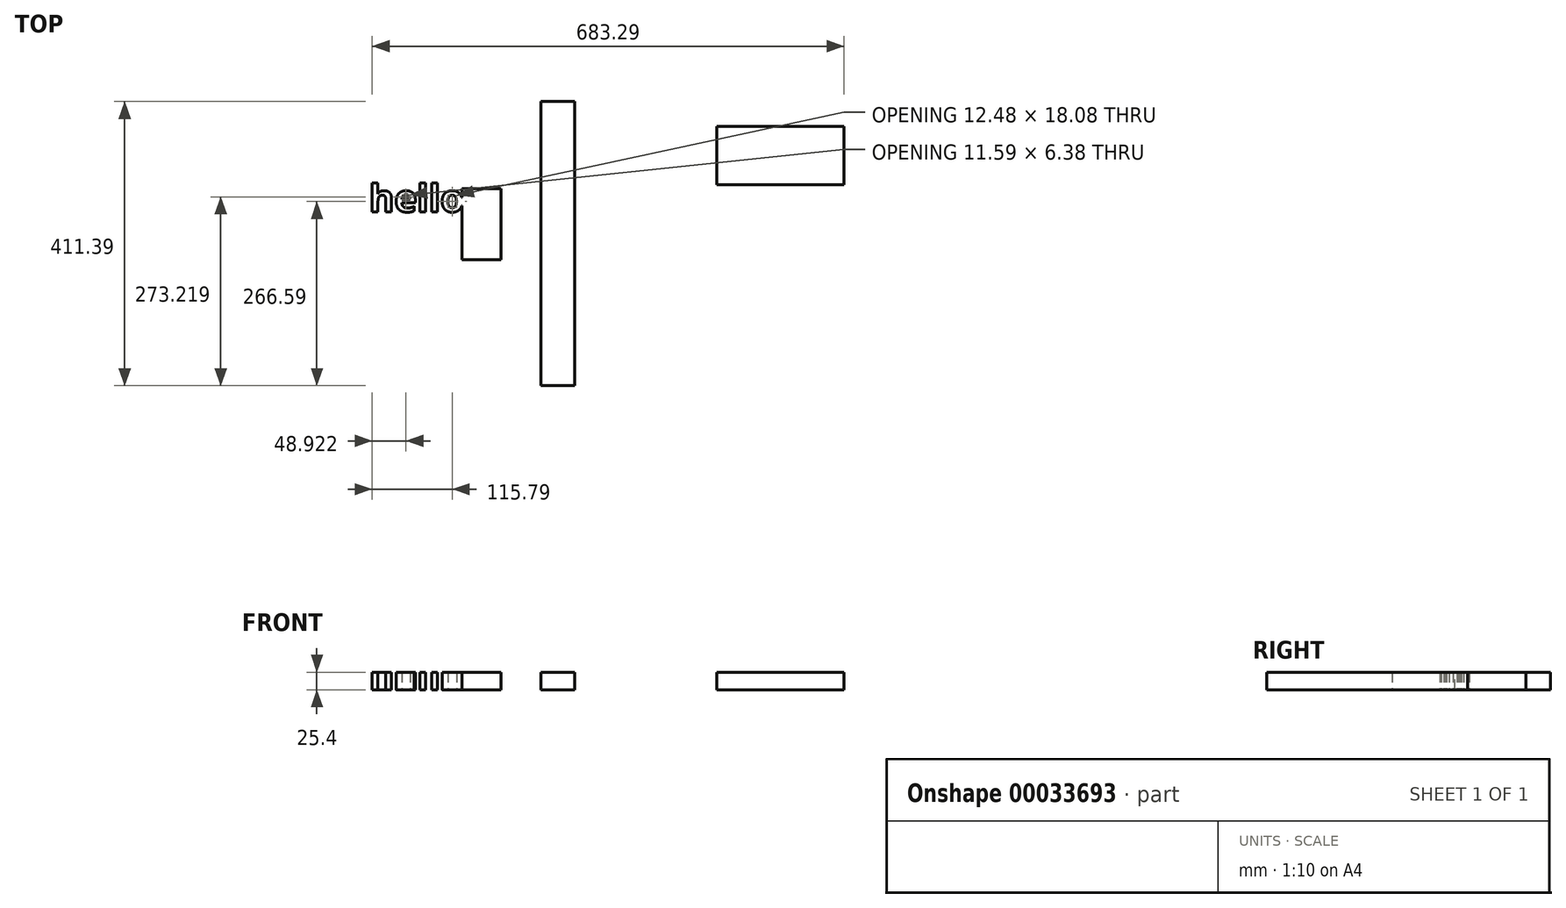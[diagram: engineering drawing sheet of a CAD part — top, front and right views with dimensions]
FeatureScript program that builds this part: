
annotation { "Feature Type Name" : "Feature", "Feature Type Description" : "" }
export const myFeature = defineFeature(function(context is Context, id is Id, definition is map)
    precondition{}
    {
        {
            var Q0;
            Q0=qCreatedBy(makeId("Top.planeOp"),FACE);
            var sketch = newSketch(context, id + "F0", { "sketchPlane" : qUnion([Q0])});
            skLineSegment(sketch, "E0.bottom", {"start": v(-276.57, -28.11) * mm, "end": v(-219.75, -28.11) * mm});
            skLineSegment(sketch, "E0.top", {"start": v(-276.57, 74.9) * mm, "end": v(-219.75, 74.9) * mm});
            skLineSegment(sketch, "E0.left", {"start": v(-276.57, -28.11) * mm, "end": v(-276.57, 74.9) * mm});
            skLineSegment(sketch, "E0.right", {"start": v(-219.75, -28.11) * mm, "end": v(-219.75, 74.9) * mm});
            skLineSegment(sketch, "E1", {"start": v(-341.55, -122.68) * mm, "end": v(-195.38, -122.68) * mm});
            skLineSegment(sketch, "E2", {"start": v(-336.67, 51.28) * mm, "end": v(-341.55, -122.68) * mm});
            skLineSegment(sketch, "E3.bottom", {"start": v(92.37, 165.15) * mm, "end": v(277.06, 165.15) * mm});
            skLineSegment(sketch, "E3.top", {"start": v(92.37, 80.88) * mm, "end": v(277.06, 80.88) * mm});
            skLineSegment(sketch, "E3.left", {"start": v(92.37, 165.15) * mm, "end": v(92.37, 80.88) * mm});
            skLineSegment(sketch, "E3.right", {"start": v(277.06, 165.15) * mm, "end": v(277.06, 80.88) * mm});
            skLineSegment(sketch, "E4", {"start": v(-171.67, 200.64) * mm, "end": v(-171.67, -206) * mm});
            skLineSegment(sketch, "E5.bottom", {"start": v(-162.07, 201.12) * mm, "end": v(-113.25, 201.12) * mm});
            skLineSegment(sketch, "E5.top", {"start": v(-162.07, -210.27) * mm, "end": v(-113.25, -210.27) * mm});
            skLineSegment(sketch, "E5.left", {"start": v(-162.07, 201.12) * mm, "end": v(-162.07, -210.27) * mm});
            skLineSegment(sketch, "E5.right", {"start": v(-113.25, 201.12) * mm, "end": v(-113.25, -210.27) * mm});
            skText(sketch, "E6", { "text": "\nhello\n", "fontName": "OpenSans-Bold.ttf"});
            const initialGuessF0  = {"E6": [-0.41056, 0.11656, 1, 0, 0.0399]};
            skSetInitialGuess(sketch, initialGuessF0);
            skSolve(sketch);
        }
        {
            var Q0;
            Q0=makeQuery(id+"F0.imprint","IMPRINT",FACE,{"disambiguationData":[TD([[makeQuery(id+"F0.imprint","IMPRINT",EDGE,{"derivedFrom":sQuery(id+"F0.wireOp",EDGE,"E3.bottom")}),-1.0]])]});
            var Q1;
            Q1=makeQuery(id+"F0.imprint","IMPRINT",FACE,{"disambiguationData":[TD([[makeQuery(id+"F0.imprint","IMPRINT",EDGE,{"derivedFrom":sQuery(id+"F0.wireOp",EDGE,"E5.bottom")}),-1.0]])]});
            var Q2;
            Q2=makeQuery(id+"F0.imprint","IMPRINT",FACE,{"disambiguationData":[TD([[makeQuery(id+"F0.imprint","IMPRINT",EDGE,{"derivedFrom":sQuery(id+"F0.wireOp",EDGE,"E6.sketch_text.stroke-0")}),-1.0]])]});
            var Q3;
            {var subQ0=sQuery(id+"F0.wireOp",EDGE,"E6.sketch_text.stroke-38");Q3=makeQuery(id+"F0.imprint","IMPRINT",FACE,{"disambiguationData":[TD([[makeQuery(id+"F0.imprint","IMPRINT",EDGE,{"derivedFrom":subQ0}),-1.0]])]});}
            var Q4;
            Q4=makeQuery(id+"F0.imprint","IMPRINT",FACE,{"disambiguationData":[TD([[makeQuery(id+"F0.imprint","IMPRINT",EDGE,{"derivedFrom":sQuery(id+"F0.wireOp",EDGE,"E6.sketch_text.stroke-41")}),-1.0]])]});
            var Q5;
            {var subQ1=sQuery(id+"F0.wireOp",EDGE,"E0.bottom");Q5=makeQuery(id+"F0.imprint","IMPRINT",FACE,{"disambiguationData":[TD([[makeQuery(id+"F0.imprint","IMPRINT",EDGE,{"derivedFrom":subQ1}),1.0]])]});}
            var Q6;
            Q6=makeQuery(id+"F0.imprint","IMPRINT",FACE,{"disambiguationData":[TD([[makeQuery(id+"F0.imprint","IMPRINT",EDGE,{"derivedFrom":sQuery(id+"F0.wireOp",EDGE,"E6.sketch_text.stroke-17")}),-1.0]])]});
            var Q7;
            Q7=makeQuery(id+"F0.imprint","IMPRINT",FACE,{"disambiguationData":[TD([[makeQuery(id+"F0.imprint","IMPRINT",EDGE,{"derivedFrom":sQuery(id+"F0.wireOp",EDGE,"E6.sketch_text.stroke-45")}),-1.0]])]});
            var Q8;
            {var subQ0=sQuery(id+"F0.wireOp",EDGE,"E6.sketch_text.stroke-53");var subQ1=sQuery(id+"F0.wireOp",EDGE,"E0.left");var subQ2=makeQuery(id+"F0.imprint","INTERSECT",VERTEX,{"derivedFrom":[subQ1,subQ0]});Q8=makeQuery(id+"F0.imprint","IMPRINT",FACE,{"disambiguationData":[TD([[makeQuery(id+"F0.imprint","IMPRINT",EDGE,{"disambiguationData":[TD([[subQ2,-1.0]])],"derivedFrom":subQ1}),-1.0]])]});}
            extrude(context, id + "F1", {"entities" : qUnion([Q0, Q1, Q2, Q3, Q4, Q5, Q6, Q7, Q8]), "depth" : 25.4 * mm});
        }
    });
